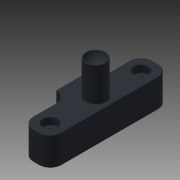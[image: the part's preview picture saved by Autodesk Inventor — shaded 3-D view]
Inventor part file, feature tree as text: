
AUTODESK INVENTOR PART (.ipt)
format: ipt  version: 2020.3 (Build 243373000, 373)  size: 272,384 bytes
history: native  units: in
note: dims shown in document units (in); Inventor stores cm internally (conversion verified against a paired STEP export)
features: sketch x6, hole x3, extrude x2, fillet x2, revolve x1
ambient origin geometry x8: Origin, YZ Plane, XZ Plane, XY Plane, X Axis, Y Axis, Z Axis, Center Point
bodies: Solid1 (feature_tree)
feature tree (14):
  revolve  "Revolution1"  [1 undecoded]
  hole  "Hole4"  [1 undecoded]
  extrude  "Extrusion1"  Depth=0.75in
  hole  "Hole3"  [1 undecoded]
  extrude  "Extrusion2"  Depth=2.0in
  hole  "Hole5"  [1 undecoded]
  fillet  "Fillet1"  Radius=0.016in
  fillet  "Fillet2"  Radius=0.625in
  sketch  "Sketch1"  dims[d0=0.3957in d1=0.0394in]
  sketch  "Sketch3"  dims[d2=0.4331in d3=0.625in]
  sketch  "Sketch4"  dims[d4=0.625in d5=0.75in]
  sketch  "Sketch5"  dims[d6=90.0deg d23=2.625in]
  sketch  "Sketch7"  dims[d24=0.625in d25=0.0in d26=2.0in]
  sketch  "Sketch8"  dims[d27=0.177in d28=0.273in d29=0.313in d30=0.164in d31=0.5635in d32=0.6in d33=0.8108in d34=0.25in d35=0.016in d36=0.05in d37=0.75in d38=0.375in d39=0.25in d40=0.5635in d41=1.0625in d42=0.8108in d43=0.625in d44=0.25in d45=0.0in d46=0.313in d47=0.273in d48=0.0246in d49=0.327in d50=0.375in d51=0.25in d52=0.5635in d53=0.65in d54=0.0in d55=0.012in]
note: 4 required parameter values undecoded (feature->parameter linkage not recoverable at this tier; creation-order binding heuristic only, values carry confidence <= 0.55)